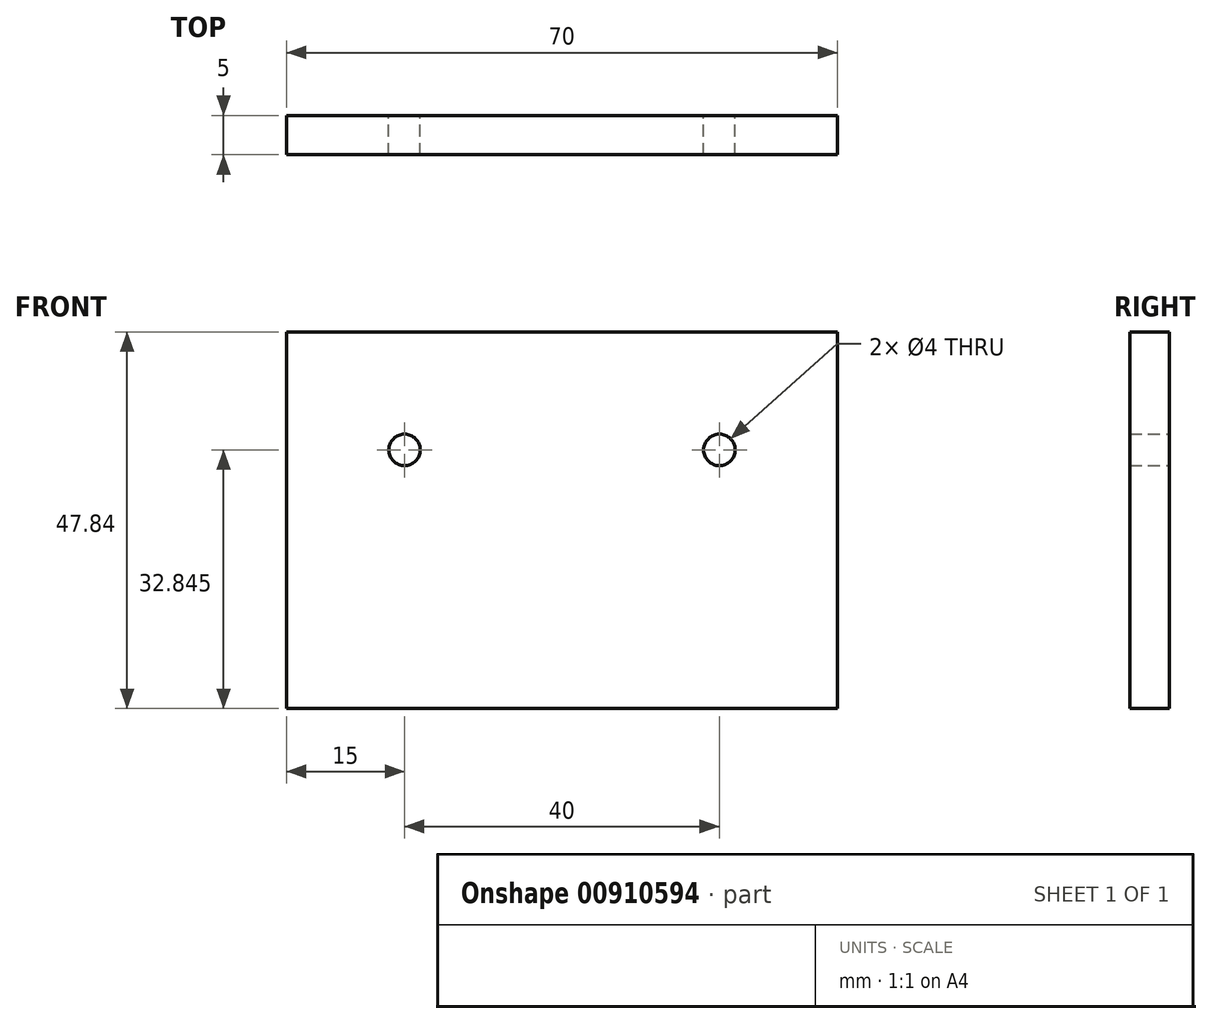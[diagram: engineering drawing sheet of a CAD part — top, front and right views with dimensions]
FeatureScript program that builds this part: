
annotation { "Feature Type Name" : "Feature", "Feature Type Description" : "" }
export const myFeature = defineFeature(function(context is Context, id is Id, definition is map)
    precondition{}
    {
        {
            var Q0;
            Q0=qCreatedBy(makeId("Front.planeOp"),FACE);
            var sketch = newSketch(context, id + "F0", { "sketchPlane" : qUnion([Q0])});
            skLineSegment(sketch, "E0.bottom", {"start": v(35, 23.93) * mm, "end": v(-35, 23.93) * mm});
            skLineSegment(sketch, "E0.top", {"start": v(35, -23.93) * mm, "end": v(-35, -23.93) * mm});
            skLineSegment(sketch, "E0.left", {"start": v(35, 23.93) * mm, "end": v(35, -23.93) * mm});
            skLineSegment(sketch, "E0.right", {"start": v(-35, 23.93) * mm, "end": v(-35, -23.93) * mm});
            skPoint(sketch, "E0.middle", {"position": v(0, 0) * mm});
            skSolve(sketch);
        }
        {
            var Q0;
            Q0 = qSketchRegion(id + "F0", true);
            extrude(context, id + "F1", {"entities" : qUnion([Q0]), "depth" : 5 * mm, "offsetDistance" : 25 * mm});
        }
        {
            var Q0;
            Q0=makeQuery(id+"F1.opExtrude","CAP_FACE",FACE,{"disambiguationData":[OSD([sQuery(id+"F0.wireOp",EDGE,"E0.bottom"),sQuery(id+"F0.wireOp",EDGE,"E0.top"),sQuery(id+"F0.wireOp",EDGE,"E0.left"),sQuery(id+"F0.wireOp",EDGE,"E0.right")])],"isStart":true});
            var sketch = newSketch(context, id + "F2", { "sketchPlane" : qUnion([Q0])});
            skPoint(sketch, "E1.oppositeSnap0", {"position": v(-37.5, 8.54) * mm});
            skPoint(sketch, "E2.orphan", {"position": v(-45, 8.54) * mm});
            skCircle(sketch, "E3", {"center": v(-20, 8.93) * mm, "radius": 2 * mm});
            skCircle(sketch, "E4", {"center": v(20, 8.93) * mm, "radius": 2 * mm});
            skPoint(sketch, "E5.center.orphan", {"position": v(-30, 8.54) * mm});
            skPoint(sketch, "E6.center.orphan", {"position": v(30, 8.54) * mm});
            skSolve(sketch);
        }
        {
            var Q0;
            Q0 = qSketchRegion(id + "F2", true);
            extrude(context, id + "F3", {"entities" : qUnion([Q0]), "operationType" : NewBodyOperationType.REMOVE, "oppositeDirection" : true, "depth" : 25 * mm, "offsetDistance" : 25 * mm});
        }
    });
